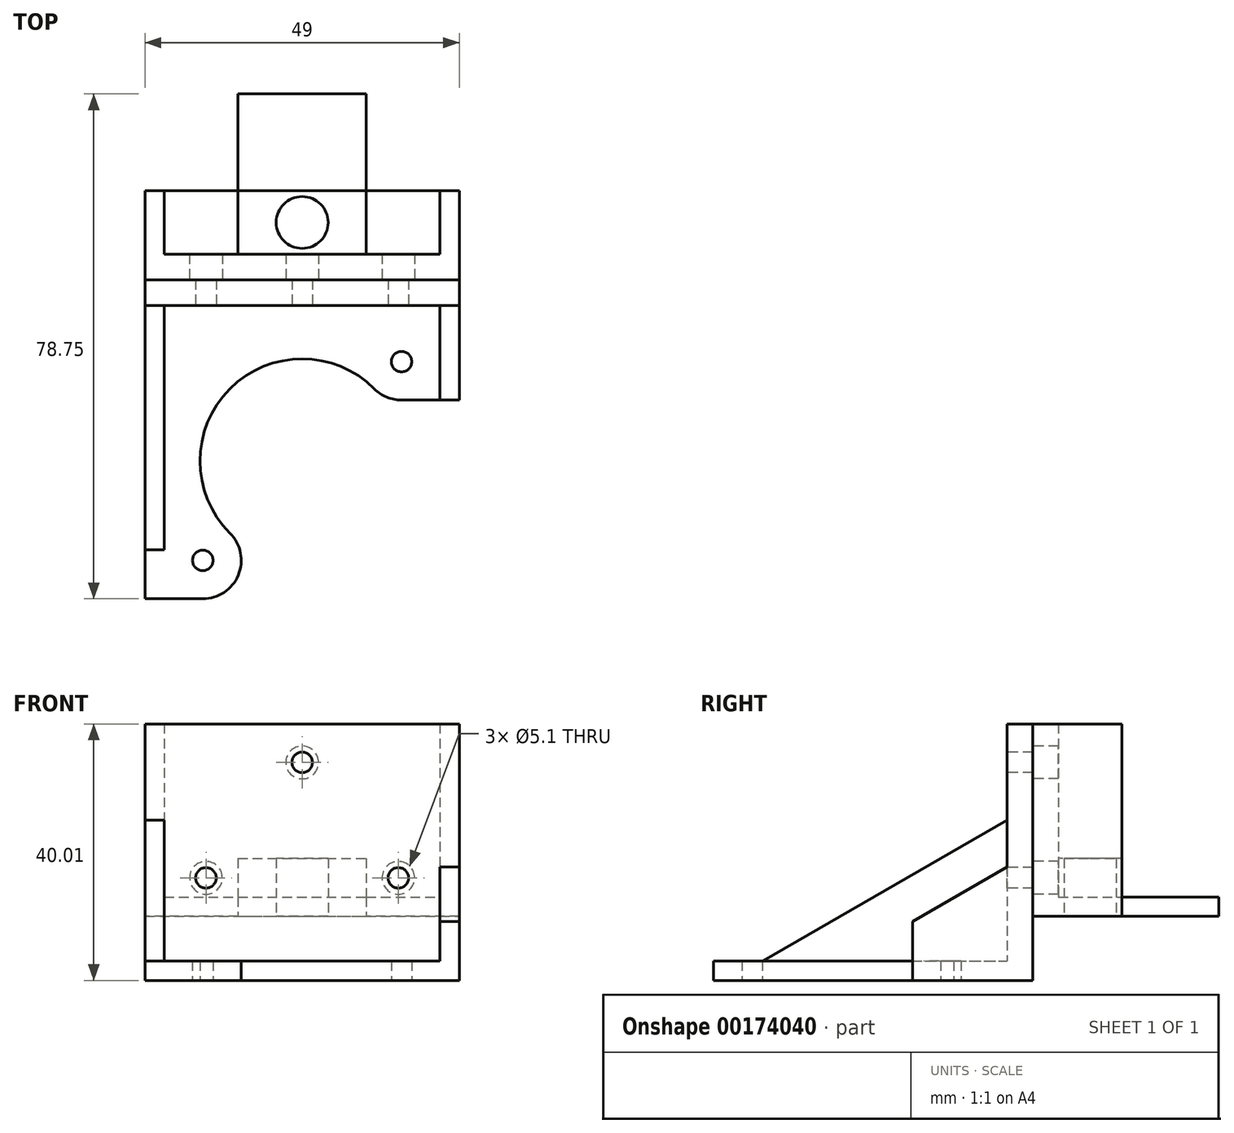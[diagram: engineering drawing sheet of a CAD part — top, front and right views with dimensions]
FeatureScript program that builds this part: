
annotation { "Feature Type Name" : "Feature", "Feature Type Description" : "" }
export const myFeature = defineFeature(function(context is Context, id is Id, definition is map)
    precondition{}
    {
        {
            var Q0;
            Q0=qCreatedBy(makeId("Top.planeOp"),FACE);
            var sketch = newSketch(context, id + "F0", { "sketchPlane" : qUnion([Q0])});
            skLineSegment(sketch, "E0.bottom", {"start": v(-10, 12.5) * mm, "end": v(10, 12.5) * mm});
            skLineSegment(sketch, "E0.top", {"start": v(-10, -12.5) * mm, "end": v(10, -12.5) * mm});
            skLineSegment(sketch, "E0.left", {"start": v(-10, 12.5) * mm, "end": v(-10, -12.5) * mm});
            skLineSegment(sketch, "E0.right", {"start": v(10, 12.5) * mm, "end": v(10, -12.5) * mm});
            skPoint(sketch, "E1", {"position": v(0, 12.5) * mm});
            skPoint(sketch, "E2", {"position": v(-10, 0) * mm});
            skSolve(sketch);
        }
        {
            var Q0;
            Q0=qSketchRegion(id+"F0",true);
            extrude(context, id + "F1", {"entities" : qUnion([Q0]), "depth" : 3 * mm});
        }
        {
            var Q0;
            Q0=qCreatedBy(makeId("Top.planeOp"),FACE);
            var sketch = newSketch(context, id + "F2", { "sketchPlane" : qUnion([Q0])});
            skLineSegment(sketch, "E3.0", {"start": v(-10, -2.6) * mm, "end": v(10, -2.6) * mm});
            skLineSegment(sketch, "E4.0", {"start": v(-10, -2.6) * mm, "end": v(-10, -12.5) * mm});
            skLineSegment(sketch, "E5.0", {"start": v(10, -2.6) * mm, "end": v(10, -12.5) * mm});
            skPoint(sketch, "E6.orphan", {"position": v(-10, 12.5) * mm});
            skPoint(sketch, "E7.orphan", {"position": v(10, 12.5) * mm});
            skCircle(sketch, "E8", {"center": v(0, -7.55) * mm, "radius": 4.05 * mm, "construction": true});
            skLineSegment(sketch, "E9", {"start": v(10, -2.6) * mm, "end": v(10, -7.5) * mm});
            skLineSegment(sketch, "E10", {"start": v(-10, -2.6) * mm, "end": v(-10, -6.8) * mm});
            skLineSegment(sketch, "E11.0", {"start": v(-10, -12.5) * mm, "end": v(10, -12.5) * mm});
            skSolve(sketch);
        }
        {
            var Q0;
            Q0=qSketchRegion(id+"F2",true);
            var Q1;
            Q1=qConstructionFilter(qBodyType(qCreatedBy(id+"F2",EDGE),BodyType.WIRE),ConstructionObject.NO);
            extrude(context, id + "F3", {"entities" : qUnion([Q0]), "operationType" : NewBodyOperationType.ADD, "surfaceEntities" : qUnion([Q1]), "depth" : 9 * mm});
        }
        {
            var Q0;
            Q0=makeQuery(id+"F0.imprint","IMPRINT",FACE,{"disambiguationData":[TD([[makeQuery(id+"F0.imprint","IMPRINT",EDGE,{"derivedFrom":sQuery(id+"F0.wireOp",EDGE,"E0.bottom")}),-1.0]])]});
            var sketch = newSketch(context, id + "F4", { "sketchPlane" : qUnion([Q0])});
            skLineSegment(sketch, "E12.0", {"start": v(-10, -2.6) * mm, "end": v(10, -2.6) * mm, "construction": true});
            skLineSegment(sketch, "E13", {"start": v(-24.5, -2.6) * mm, "end": v(-24.5, -16.5) * mm});
            skLineSegment(sketch, "E14", {"start": v(-24.5, -16.5) * mm, "end": v(24.5, -16.5) * mm});
            skLineSegment(sketch, "E15", {"start": v(24.5, -16.5) * mm, "end": v(24.5, -2.6) * mm});
            skLineSegment(sketch, "E16", {"start": v(24.5, -2.6) * mm, "end": v(21.5, -2.6) * mm});
            skLineSegment(sketch, "E17", {"start": v(21.5, -2.6) * mm, "end": v(21.5, -12.5) * mm});
            skLineSegment(sketch, "E18", {"start": v(21.5, -12.5) * mm, "end": v(-21.5, -12.5) * mm});
            skLineSegment(sketch, "E19", {"start": v(-21.5, -12.5) * mm, "end": v(-21.5, -2.6) * mm});
            skLineSegment(sketch, "E20", {"start": v(-21.5, -2.6) * mm, "end": v(-24.5, -2.6) * mm});
            skPoint(sketch, "E21", {"position": v(0, -12.5) * mm});
            skSolve(sketch);
        }
        {
            var Q0;
            Q0 = qSketchRegion(id + "F4", true);
            extrude(context, id + "F5", {"entities" : qUnion([Q0]), "operationType" : NewBodyOperationType.ADD, "depth" : 30 * mm});
        }
        {
            var Q0;
            Q0=makeQuery(id+"F5.boolean.opBoolean","MERGE",FACE,{"derivedFrom":[makeQuery(id+"F1.opExtrude","CAP_FACE",FACE,{"disambiguationData":[OSD([sQuery(id+"F0.wireOp",EDGE,"E0.bottom"),sQuery(id+"F0.wireOp",EDGE,"E0.top"),sQuery(id+"F0.wireOp",EDGE,"E0.left"),sQuery(id+"F0.wireOp",EDGE,"E0.right")])],"isStart":true}),makeQuery(id+"F5.opExtrude","CAP_FACE",FACE,{"disambiguationData":[OSD([sQuery(id+"F4.wireOp",EDGE,"E13"),sQuery(id+"F4.wireOp",EDGE,"E14"),sQuery(id+"F4.wireOp",EDGE,"E15"),sQuery(id+"F4.wireOp",EDGE,"E16"),sQuery(id+"F4.wireOp",EDGE,"E17"),sQuery(id+"F4.wireOp",EDGE,"E18"),sQuery(id+"F4.wireOp",EDGE,"E19"),sQuery(id+"F4.wireOp",EDGE,"E20")])],"isStart":true})]});
            var sketch = newSketch(context, id + "F6", { "sketchPlane" : qUnion([Q0])});
            skLineSegment(sketch, "E22.bottom", {"start": v(-24.5, 16.5) * mm, "end": v(24.5, 16.5) * mm});
            skLineSegment(sketch, "E22.top", {"start": v(-24.5, 2.6) * mm, "end": v(24.5, 2.6) * mm});
            skLineSegment(sketch, "E22.left", {"start": v(-24.5, 16.5) * mm, "end": v(-24.5, 2.6) * mm});
            skLineSegment(sketch, "E22.right", {"start": v(24.5, 16.5) * mm, "end": v(24.5, 2.6) * mm});
            skSolve(sketch);
        }
        {
            var Q0;
            Q0 = qSketchRegion(id + "F6", true);
            extrude(context, id + "F7", {"entities" : qUnion([Q0]), "operationType" : NewBodyOperationType.ADD, "oppositeDirection" : true, "depth" : 3 * mm});
        }
        {
            var Q0;
            Q0=qCreatedBy(makeId("Top.planeOp"),FACE);
            var sketch = newSketch(context, id + "F8", { "sketchPlane" : qUnion([Q0])});
            skCircle(sketch, "E23.0", {"center": v(0, -7.55) * mm, "radius": 4.05 * mm});
            skSolve(sketch);
        }
        {
            var Q0;
            Q0=qSketchRegion(id+"F8",true);
            var Q1;
            Q1=qConstructionFilter(qBodyType(qCreatedBy(id+"F8",EDGE),BodyType.WIRE),ConstructionObject.NO);
            var Q2;
            Q2=makeQuery(id+"F3.opExtrude","CAP_FACE",FACE,{"disambiguationData":[OSD([sQuery(id+"F2.wireOp",EDGE,"E3.0"),sQuery(id+"F2.wireOp",EDGE,"a2q0104G-Bl7I-Rjex-EUNp-YHxzSH3oDlM2"),sQuery(id+"F2.wireOp",EDGE,"E9"),sQuery(id+"F2.wireOp",EDGE,"E10")])],"isStart":false});
            var Q3;
            Q3=makeQuery(id+"F1.opExtrude","SWEPT_BODY",BODY,{"disambiguationData":[OSD([sQuery(id+"F0.wireOp",EDGE,"E0.bottom"),sQuery(id+"F0.wireOp",EDGE,"E0.top"),sQuery(id+"F0.wireOp",EDGE,"E0.left"),sQuery(id+"F0.wireOp",EDGE,"E0.right")])]});
            extrude(context, id + "F9", {"entities" : qUnion([Q0]), "operationType" : NewBodyOperationType.REMOVE, "surfaceEntities" : qUnion([Q1]), "endBound" : BoundingType.UP_TO_SURFACE, "endBoundEntityFace" : qUnion([Q2]), "endBoundEntityBody" : qUnion([Q3]), "depth" : 25 * mm});
        }
        {
            var Q0;
            Q0=makeQuery(id+"F5.opExtrude","SWEPT_FACE",FACE,{"disambiguationData":[OSD([sQuery(id+"F4.wireOp",EDGE,"E14")])]});
            var sketch = newSketch(context, id + "F10", { "sketchPlane" : qUnion([Q0])});
            skCircle(sketch, "E24", {"center": v(15, 6) * mm, "radius": 2.55 * mm});
            skCircle(sketch, "E25", {"center": v(-15, 6) * mm, "radius": 2.55 * mm});
            skCircle(sketch, "E26", {"center": v(0, 24) * mm, "radius": 2.55 * mm});
            skLineSegment(sketch, "E27", {"start": v(-15, 6) * mm, "end": v(15, 6) * mm, "construction": true});
            skPoint(sketch, "E28", {"position": v(0, 6) * mm});
            skSolve(sketch);
        }
        {
            var Q0;
            Q0 = qSketchRegion(id + "F10", true);
            extrude(context, id + "F11", {"entities" : qUnion([Q0]), "operationType" : NewBodyOperationType.REMOVE, "oppositeDirection" : true, "depth" : 25 * mm});
        }
        {
            var Q0;
            Q0=makeQuery(id+"F5.opExtrude","SWEPT_FACE",FACE,{"disambiguationData":[OSD([sQuery(id+"F4.wireOp",EDGE,"E14")])]});
            var sketch = newSketch(context, id + "F12", { "sketchPlane" : qUnion([Q0])});
            skLineSegment(sketch, "E29.bottom", {"start": v(-24.5, 30) * mm, "end": v(24.5, 30) * mm});
            skLineSegment(sketch, "E29.top", {"start": v(-24.5, -10) * mm, "end": v(24.5, -10) * mm});
            skLineSegment(sketch, "E29.left", {"start": v(-24.5, 30) * mm, "end": v(-24.5, -10) * mm});
            skLineSegment(sketch, "E29.right", {"start": v(24.5, 30) * mm, "end": v(24.5, -10) * mm});
            skPoint(sketch, "E30", {"position": v(0, 30) * mm});
            skSolve(sketch);
        }
        {
            var Q0;
            Q0 = qSketchRegion(id + "F12", true);
            extrude(context, id + "F13", {"entities" : qUnion([Q0]), "depth" : 4 * mm});
        }
        {
            var Q0;
            Q0=makeQuery(id+"F13.opExtrude","CAP_FACE",FACE,{"disambiguationData":[OSD([sQuery(id+"F12.wireOp",EDGE,"E29.bottom"),sQuery(id+"F12.wireOp",EDGE,"E29.top"),sQuery(id+"F12.wireOp",EDGE,"E29.left"),sQuery(id+"F12.wireOp",EDGE,"E29.right")])],"isStart":false});
            var sketch = newSketch(context, id + "F14", { "sketchPlane" : qUnion([Q0])});
            skPoint(sketch, "E31.0", {"position": v(-15, 6) * mm});
            skPoint(sketch, "E32.0", {"position": v(0, 24) * mm});
            skPoint(sketch, "E33.0", {"position": v(15, 6) * mm});
            skCircle(sketch, "E34", {"center": v(-15, 6) * mm, "radius": 1.6 * mm});
            skCircle(sketch, "E35", {"center": v(0, 24) * mm, "radius": 1.6 * mm});
            skCircle(sketch, "E36", {"center": v(15, 6) * mm, "radius": 1.6 * mm});
            skSolve(sketch);
        }
        {
            var Q0;
            Q0 = qSketchRegion(id + "F14", true);
            extrude(context, id + "F15", {"entities" : qUnion([Q0]), "operationType" : NewBodyOperationType.REMOVE, "endBound" : BoundingType.THROUGH_ALL, "oppositeDirection" : true, "depth" : 25 * mm});
        }
        {
            var Q0;
            Q0=makeQuery(id+"F13.opExtrude","SWEPT_FACE",FACE,{"disambiguationData":[OSD([sQuery(id+"F12.wireOp",EDGE,"E29.top")])]});
            var sketch = newSketch(context, id + "F16", { "sketchPlane" : qUnion([Q0])});
            skLineSegment(sketch, "E37.bottom", {"start": v(-21.5, 66.5) * mm, "end": v(21.5, 66.5) * mm, "construction": true});
            skLineSegment(sketch, "E37.top", {"start": v(-21.5, 23) * mm, "end": v(21.5, 23) * mm, "construction": true});
            skLineSegment(sketch, "E37.left", {"start": v(-21.5, 66.5) * mm, "end": v(-21.5, 23) * mm, "construction": true});
            skLineSegment(sketch, "E37.right", {"start": v(21.5, 66.5) * mm, "end": v(21.5, 23) * mm, "construction": true});
            skLineSegment(sketch, "E38.bottom", {"start": v(-15.5, 60.25) * mm, "end": v(15.5, 60.25) * mm, "construction": true});
            skLineSegment(sketch, "E38.top", {"start": v(-15.5, 29.25) * mm, "end": v(15.5, 29.25) * mm, "construction": true});
            skLineSegment(sketch, "E38.left", {"start": v(-15.5, 60.25) * mm, "end": v(-15.5, 29.25) * mm, "construction": true});
            skLineSegment(sketch, "E38.right", {"start": v(15.5, 60.25) * mm, "end": v(15.5, 29.25) * mm, "construction": true});
            skPoint(sketch, "E39", {"position": v(-21.5, 44.75) * mm});
            skPoint(sketch, "E40", {"position": v(-15.5, 44.75) * mm});
            skPoint(sketch, "E41", {"position": v(0, 60.25) * mm});
            skPoint(sketch, "E42", {"position": v(0, 66.5) * mm});
            skCircle(sketch, "E43", {"center": v(-15.5, 60.25) * mm, "radius": 1.6 * mm});
            skCircle(sketch, "E44", {"center": v(15.5, 29.25) * mm, "radius": 1.6 * mm});
            skArc(sketch, "E45", {"start": v(-11.26, 56) * mm, "mid": v(-11.26, 33.5) * mm, "end": v(11.26, 33.5) * mm});
            skLineSegment(sketch, "E46.bottom", {"start": v(-24.5, 20.5) * mm, "end": v(24.5, 20.5) * mm});
            skLineSegment(sketch, "E46.top", {"start": v(-24.5, 66.25) * mm, "end": v(-15.5, 66.25) * mm});
            skLineSegment(sketch, "E46.left", {"start": v(-24.5, 20.5) * mm, "end": v(-24.5, 66.25) * mm});
            skLineSegment(sketch, "E46.right", {"start": v(24.5, 20.5) * mm, "end": v(24.5, 35.25) * mm});
            skArc(sketch, "E47", {"start": v(15.5, 35.25) * mm, "mid": v(13.2, 34.8) * mm, "end": v(11.26, 33.5) * mm});
            skArc(sketch, "E48", {"start": v(-11.26, 56) * mm, "mid": v(-9.96, 62.55) * mm, "end": v(-15.5, 66.25) * mm});
            skLineSegment(sketch, "E49", {"start": v(15.5, 35.25) * mm, "end": v(24.5, 35.25) * mm});
            skSolve(sketch);
        }
        {
            var Q0;
            Q0 = qSketchRegion(id + "F16", true);
            extrude(context, id + "F17", {"entities" : qUnion([Q0]), "operationType" : NewBodyOperationType.ADD, "oppositeDirection" : true, "depth" : 3 * mm});
        }
        {
            var Q0;
            Q0=makeQuery(id+"F16.imprint","IMPRINT",FACE,{"disambiguationData":[TD([[makeQuery(id+"F16.imprint","IMPRINT",EDGE,{"derivedFrom":sQuery(id+"F16.wireOp",EDGE,"E43")}),-1.0]])]});
            var sketch = newSketch(context, id + "F18", { "sketchPlane" : qUnion([Q0])});
            skLineSegment(sketch, "E50.0", {"start": v(24.5, 20.5) * mm, "end": v(24.5, 35.25) * mm});
            skLineSegment(sketch, "E51.0", {"start": v(-24.5, 20.5) * mm, "end": v(-24.5, 66.25) * mm});
            skLineSegment(sketch, "E52.bottom", {"start": v(-24.5, 66.25) * mm, "end": v(-21.5, 66.25) * mm});
            skLineSegment(sketch, "E52.top", {"start": v(-24.5, 20.5) * mm, "end": v(-21.5, 20.5) * mm});
            skLineSegment(sketch, "E52.left", {"start": v(-24.5, 66.25) * mm, "end": v(-24.5, 20.5) * mm});
            skLineSegment(sketch, "E52.right", {"start": v(-21.5, 66.25) * mm, "end": v(-21.5, 20.5) * mm});
            skPoint(sketch, "E53.0.start.orphan", {"position": v(-21.5, 66.5) * mm});
            skLineSegment(sketch, "E54.bottom", {"start": v(24.5, 35.25) * mm, "end": v(21.5, 35.25) * mm});
            skLineSegment(sketch, "E54.top", {"start": v(24.5, 20.5) * mm, "end": v(21.5, 20.5) * mm});
            skLineSegment(sketch, "E54.left", {"start": v(24.5, 35.25) * mm, "end": v(24.5, 20.5) * mm});
            skLineSegment(sketch, "E54.right", {"start": v(21.5, 35.25) * mm, "end": v(21.5, 20.5) * mm});
            skSolve(sketch);
        }
        {
            var Q0;
            Q0 = qSketchRegion(id + "F18", true);
            extrude(context, id + "F19", {"entities" : qUnion([Q0]), "operationType" : NewBodyOperationType.ADD, "oppositeDirection" : true, "depth" : 25 * mm});
        }
        {
            var Q0;
            Q0=makeQuery(id+"F19.boolean.opBoolean","MERGE",FACE,{"derivedFrom":[makeQuery(id+"F17.opExtrude","SWEPT_FACE",FACE,{"disambiguationData":[OSD([sQuery(id+"F16.wireOp",EDGE,"E46.right")])]}),makeQuery(id+"F19.opExtrude","SWEPT_FACE",FACE,{"disambiguationData":[OSD([sQuery(id+"F18.wireOp",EDGE,"WZuMoOde-d7dr-u5JS-0lOJ-TiRcxLhmbwG5.left")])]})]});
            var sketch = newSketch(context, id + "F20", { "sketchPlane" : qUnion([Q0])});
            skLineSegment(sketch, "E55.bottom", {"start": v(-35.25, 15) * mm, "end": v(-20.5, 15) * mm});
            skLineSegment(sketch, "E55.left", {"start": v(-35.25, 15) * mm, "end": v(-35.25, -0.83) * mm});
            skLineSegment(sketch, "E55.right", {"start": v(-20.5, 15) * mm, "end": v(-20.5, 7.68) * mm});
            skLineSegment(sketch, "E56", {"start": v(-35.25, -0.83) * mm, "end": v(-20.5, 7.68) * mm});
            skSolve(sketch);
        }
        {
            var Q0;
            Q0 = qSketchRegion(id + "F20", true);
            var Q1;
            Q1=makeQuery(id+"F19.opExtrude","SWEPT_FACE",FACE,{"disambiguationData":[OSD([sQuery(id+"F18.wireOp",EDGE,"E54.right")])]});
            extrude(context, id + "F21", {"entities" : qUnion([Q0]), "operationType" : NewBodyOperationType.REMOVE, "endBound" : BoundingType.UP_TO_SURFACE, "oppositeDirection" : true, "endBoundEntityFace" : qUnion([Q1]), "depth" : 25 * mm});
        }
        {
            var Q0;
            Q0=makeQuery(id+"F19.boolean.opBoolean","MERGE",FACE,{"derivedFrom":[makeQuery(id+"F17.opExtrude","SWEPT_FACE",FACE,{"disambiguationData":[OSD([sQuery(id+"F16.wireOp",EDGE,"E46.left")])]}),makeQuery(id+"F19.opExtrude","SWEPT_FACE",FACE,{"disambiguationData":[OSD([sQuery(id+"F18.wireOp",EDGE,"E52.left")])]})]});
            var sketch = newSketch(context, id + "F22", { "sketchPlane" : qUnion([Q0])});
            skLineSegment(sketch, "E57.bottom", {"start": v(20.5, 15) * mm, "end": v(66.25, 15) * mm});
            skLineSegment(sketch, "E58", {"start": v(20.5, 15) * mm, "end": v(58.6, -7) * mm});
            skPoint(sketch, "E59.0", {"position": v(66.25, -7) * mm});
            skLineSegment(sketch, "E60", {"start": v(58.6, -7) * mm, "end": v(66.25, -7) * mm});
            skLineSegment(sketch, "E61", {"start": v(66.25, -7) * mm, "end": v(66.25, 15) * mm});
            skSolve(sketch);
        }
        {
            var Q0;
            Q0 = qSketchRegion(id + "F22", true);
            extrude(context, id + "F23", {"entities" : qUnion([Q0]), "operationType" : NewBodyOperationType.REMOVE, "oppositeDirection" : true, "depth" : 25 * mm});
        }
    });
